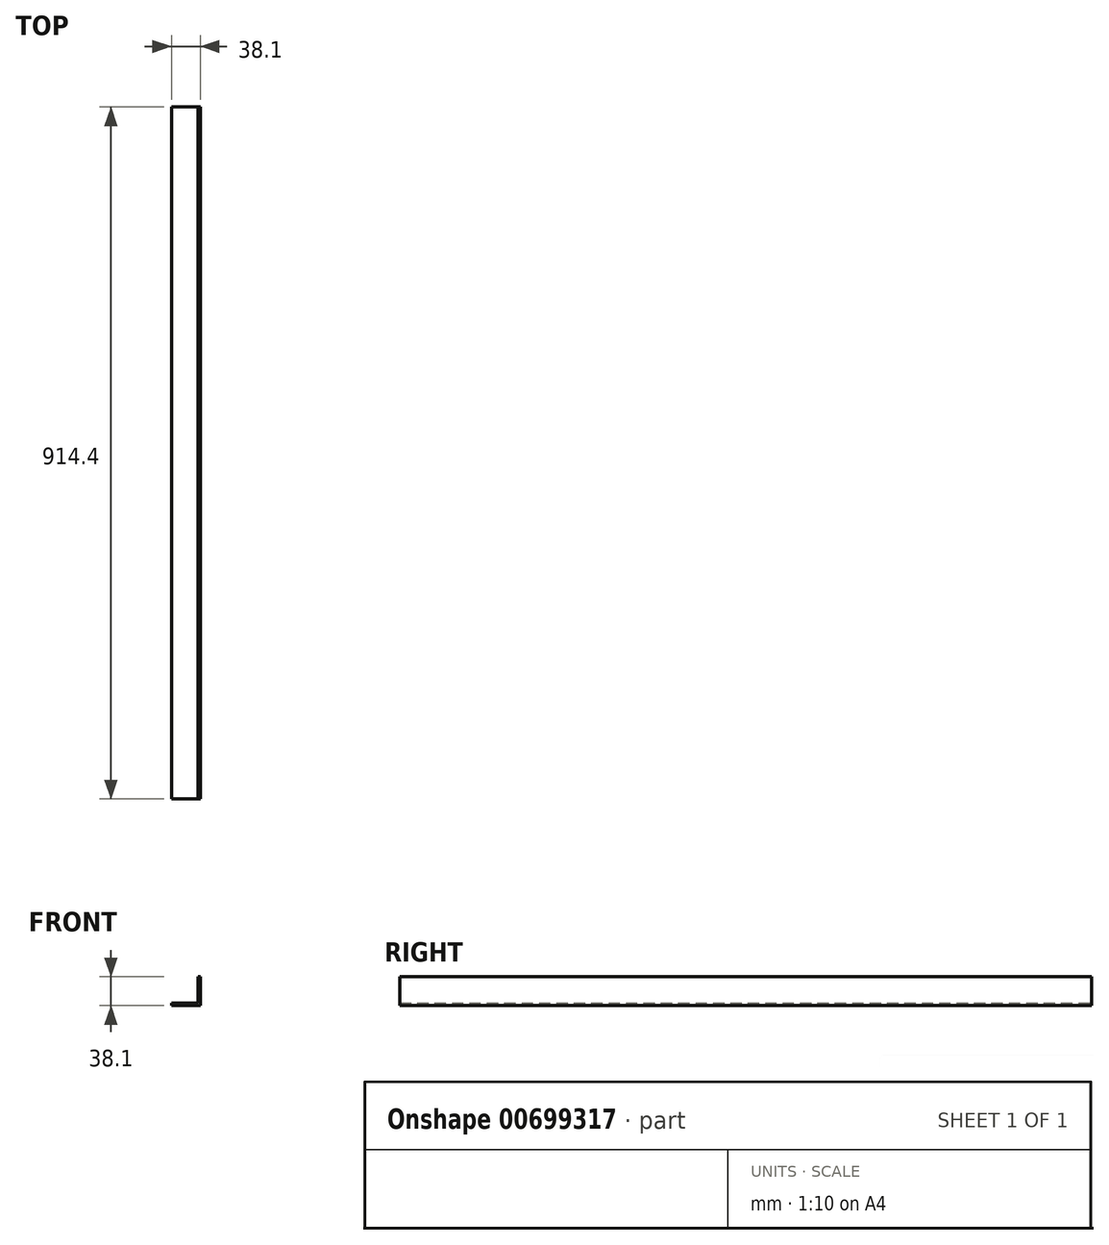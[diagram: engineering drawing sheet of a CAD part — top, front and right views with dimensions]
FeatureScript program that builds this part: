
annotation { "Feature Type Name" : "Feature", "Feature Type Description" : "" }
export const myFeature = defineFeature(function(context is Context, id is Id, definition is map)
    precondition{}
    {
        {
            var Q0;
            Q0=qCreatedBy(makeId("Front.planeOp"),FACE);
            var sketch = newSketch(context, id + "F0", { "sketchPlane" : qUnion([Q0])});
            skLineSegment(sketch, "E0", {"start": v(0, 0) * mm, "end": v(38.1, 0) * mm});
            skLineSegment(sketch, "E1", {"start": v(38.1, 0) * mm, "end": v(38.1, 38.1) * mm});
            skLineSegment(sketch, "E2", {"start": v(38.1, 38.1) * mm, "end": v(34.92, 38.1) * mm});
            skLineSegment(sketch, "E3", {"start": v(34.92, 38.1) * mm, "end": v(34.93, 3.18) * mm});
            skLineSegment(sketch, "E4", {"start": v(34.93, 3.18) * mm, "end": v(0, 3.18) * mm});
            skLineSegment(sketch, "E5", {"start": v(0, 3.18) * mm, "end": v(0, 0) * mm});
            skSolve(sketch);
        }
        {
            var Q0;
            Q0=makeQuery(id+"F0.imprint","IMPRINT",FACE,{"disambiguationData":[TD([[makeQuery(id+"F0.imprint","IMPRINT",EDGE,{"derivedFrom":sQuery(id+"F0.wireOp",EDGE,"E0")}),1.0]])]});
            extrude(context, id + "F1", {"entities" : qUnion([Q0]), "depth" : 914.4 * mm, "offsetDistance" : 25.4 * mm});
        }
    });
